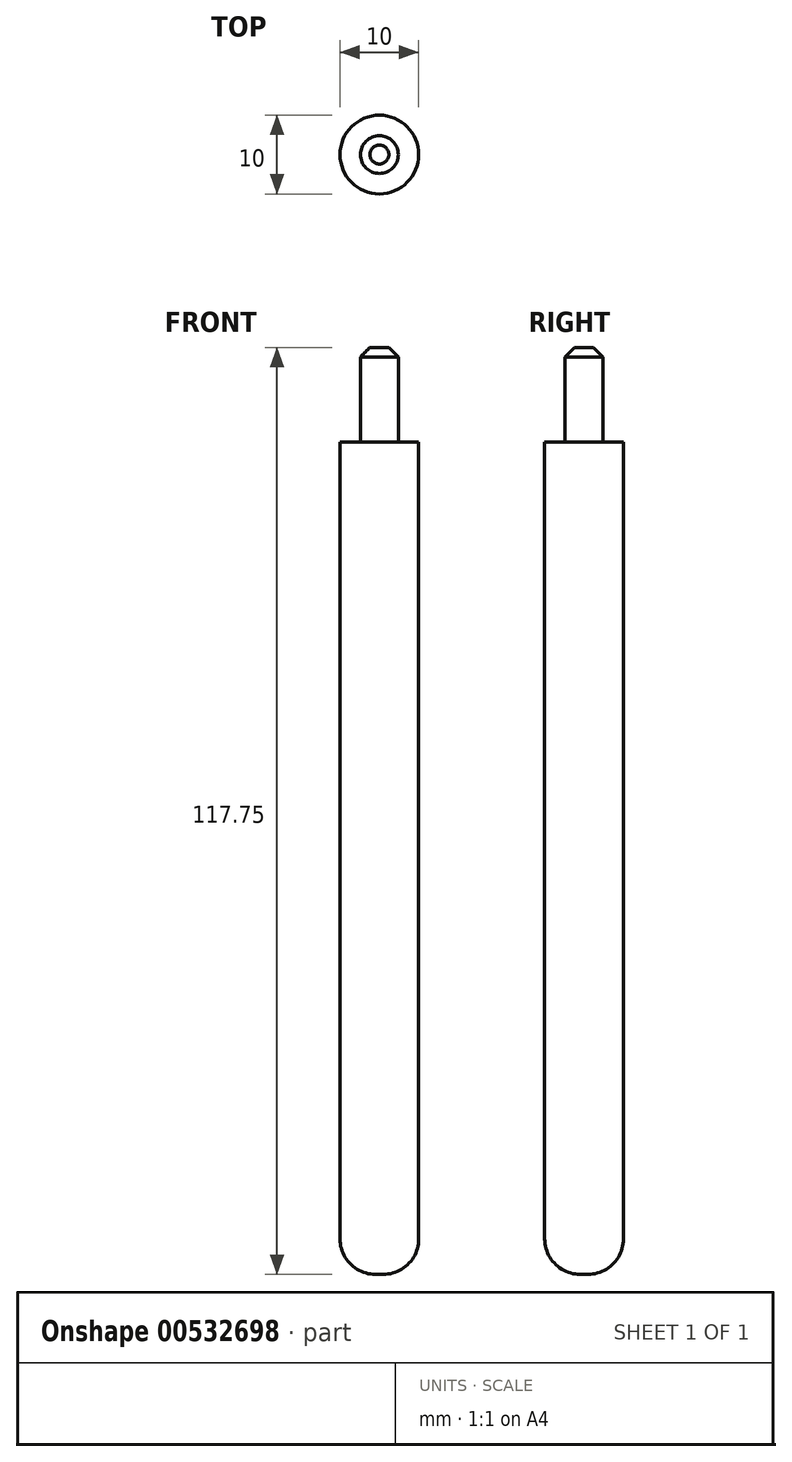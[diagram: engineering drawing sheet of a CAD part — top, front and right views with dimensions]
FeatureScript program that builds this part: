
annotation { "Feature Type Name" : "Feature", "Feature Type Description" : "" }
export const myFeature = defineFeature(function(context is Context, id is Id, definition is map)
    precondition{}
    {
        {
            var Q0;
            Q0=qCreatedBy(makeId("Front.planeOp"),FACE);
            var sketch = newSketch(context, id + "F0", { "sketchPlane" : qUnion([Q0])});
            skLineSegment(sketch, "E0", {"start": v(-5, -40.57) * mm, "end": v(-5, -146.32) * mm});
            skLineSegment(sketch, "E1", {"start": v(-5, -146.32) * mm, "end": v(0, -146.32) * mm});
            skPoint(sketch, "E2.start.orphan", {"position": v(0, 139.79) * mm});
            skLineSegment(sketch, "E3", {"start": v(-2.4, -28.57) * mm, "end": v(0, -28.57) * mm});
            skLineSegment(sketch, "E4", {"start": v(0, -28.57) * mm, "end": v(0, -146.32) * mm});
            skLineSegment(sketch, "E5", {"start": v(0, -28.57) * mm, "end": v(0, -244.68) * mm, "construction": true});
            skLineSegment(sketch, "E6", {"start": v(-2.4, -28.57) * mm, "end": v(-2.4, -40.57) * mm});
            skLineSegment(sketch, "E7", {"start": v(-2.4, -40.57) * mm, "end": v(-5, -40.57) * mm});
            skSolve(sketch);
        }
        {
            var Q0;
            Q0=makeQuery(id+"F0.imprint","IMPRINT",FACE,{"disambiguationData":[TD([[makeQuery(id+"F0.imprint","IMPRINT",EDGE,{"derivedFrom":sQuery(id+"F0.wireOp",EDGE,"E0")}),1.0]])]});
            var Q1;
            Q1=sQuery(id+"F0.wireOp",EDGE,"E5");
            revolve(context, id + "F1", {"entities" : qUnion([Q0]), "axis" : qUnion([Q1]), "revolveType" : RevolveType.FULL});
        }
        {
            var Q0;
            Q0=makeQuery(id+"F1.opRevolve","SWEPT_EDGE",EDGE,{"disambiguationData":[OSD([sQuery(id+"F0.wireOp",EDGE,"E0"),sQuery(id+"F0.wireOp",EDGE,"E1")])]});
            fillet(context, id + "F2", {"entities" : qUnion([Q0]), "radius" : 4.5 * mm, "tangentPropagation" : true, "allowEdgeOverflow" : false});
        }
        {
            var Q0;
            Q0=makeQuery(id+"F1.opRevolve","SWEPT_EDGE",EDGE,{"disambiguationData":[OSD([sQuery(id+"F0.wireOp",EDGE,"E3"),sQuery(id+"F0.wireOp",EDGE,"E6")])]});
            chamfer(context, id + "F3", {"entities" : qUnion([Q0]), "width" : 1.2 * mm, "tangentPropagation" : true});
        }
        {
            var Q0;
            Q0=makeQuery(id+"F1.opRevolve","SWEPT_EDGE",EDGE,{"disambiguationData":[OSD([sQuery(id+"F0.wireOp",EDGE,"E6"),sQuery(id+"F0.wireOp",EDGE,"E7")])]});
            fillet(context, id + "F4", {"entities" : qUnion([Q0]), "radius" : 0.2 * mm, "tangentPropagation" : true, "allowEdgeOverflow" : false});
        }
    });
